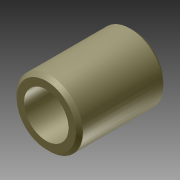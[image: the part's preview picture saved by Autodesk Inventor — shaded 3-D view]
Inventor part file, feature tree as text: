
AUTODESK INVENTOR PART (.ipt)
format: ipt  version: 2012 (Build 160160000, 160)  size: 101,376 bytes
history: native  units: in
note: dims shown in document units (in); Inventor stores cm internally (conversion verified against a paired STEP export)
features: other x35, revolve x1, sketch x1
ambient origin geometry x8: Origin, YZ Plane, XZ Plane, XY Plane, X Axis, Y Axis, Z Axis, Center Point
bodies: Solid1 (feature_tree)
feature tree (37):
  revolve  "Revolution1"  [1 undecoded]
  other  "bushing_XY"
  other  "bushing_YZ"
  other  "bushing_ZX"
  other  "bushing_X"
  other  "bushing_Y"
  other  "bushing_Z"
  other  "bushing_Center"
  other  "id1_XY"
  other  "id1_YZ"
  other  "id1_ZX"
  other  "id1_X"
  other  "id1_Y"
  other  "id1_Z"
  other  "id1_Center"
  other  "id2_XY"
  other  "id2_YZ"
  other  "id2_ZX"
  other  "id2_X"
  other  "id2_Y"
  other  "id2_Z"
  other  "id2_Center"
  other  "id3_XY"
  other  "id3_YZ"
  other  "id3_ZX"
  other  "id3_X"
  other  "id3_Y"
  other  "id3_Z"
  other  "id3_Center"
  other  "id4_XY"
  other  "id4_YZ"
  other  "id4_ZX"
  other  "id4_X"
  other  "id4_Y"
  other  "id4_Z"
  other  "id4_Center"
  sketch  "Sketch_1"  dims[d0=360.0deg]
note: 1 required parameter value undecoded (feature->parameter linkage not recoverable at this tier; creation-order binding heuristic only, values carry confidence <= 0.55)
